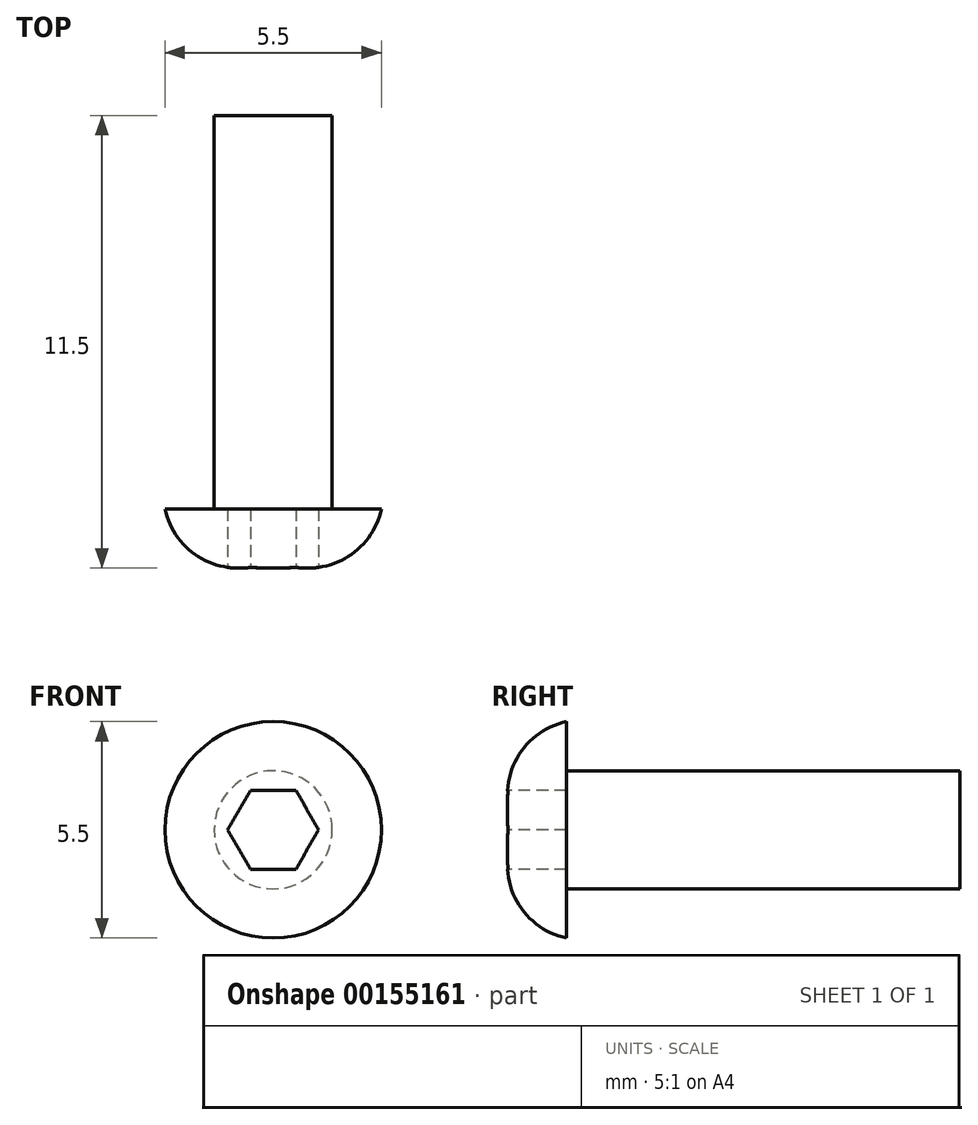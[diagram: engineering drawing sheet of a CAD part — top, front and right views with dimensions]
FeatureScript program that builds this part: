
annotation { "Feature Type Name" : "Feature", "Feature Type Description" : "" }
export const myFeature = defineFeature(function(context is Context, id is Id, definition is map)
    precondition{}
    {
        {
            var Q0;
            Q0=qCreatedBy(makeId("Front.planeOp"),FACE);
            var sketch = newSketch(context, id + "F0", { "sketchPlane" : qUnion([Q0])});
            skCircle(sketch, "E0", {"center": v(0, 0) * mm, "radius": 1.5 * mm});
            skSolve(sketch);
        }
        {
            var Q0;
            Q0=makeQuery(id+"F0.imprint","IMPRINT",FACE,{"disambiguationData":[TD([[makeQuery(id+"F0.imprint","IMPRINT",EDGE,{"derivedFrom":sQuery(id+"F0.wireOp",EDGE,"E0")}),1.0]])]});
            extrude(context, id + "F1", {"entities" : qUnion([Q0]), "depth" : 10 * mm});
        }
        {
            var Q0;
            Q0=makeQuery(id+"F1.opExtrude","CAP_FACE",FACE,{"disambiguationData":[OSD([sQuery(id+"F0.wireOp",EDGE,"E0")])],"isStart":false});
            var sketch = newSketch(context, id + "F2", { "sketchPlane" : qUnion([Q0])});
            skCircle(sketch, "E1", {"center": v(0, 0) * mm, "radius": 2.75 * mm});
            skSolve(sketch);
        }
        {
            var Q0;
            Q0 = qSketchRegion(id + "F2", true);
            extrude(context, id + "F3", {"entities" : qUnion([Q0]), "operationType" : NewBodyOperationType.ADD, "depth" : 1.5 * mm});
        }
        {
            var Q0;
            Q0=makeQuery(id+"F3.opExtrude","CAP_FACE",FACE,{"disambiguationData":[OSD([sQuery(id+"F2.wireOp",EDGE,"E1")])],"isStart":false});
            var sketch = newSketch(context, id + "F4", { "sketchPlane" : qUnion([Q0])});
            skCircle(sketch, "E2.cCircle", {"center": v(0, 0) * mm, "radius": 1 * mm, "construction": true});
            skLineSegment(sketch, "E2.0", {"start": v(0.58, -1) * mm, "end": v(-0.58, -1) * mm});
            skLineSegment(sketch, "E2.1", {"start": v(-0.58, -1) * mm, "end": v(-1.15, 0) * mm});
            skLineSegment(sketch, "E2.2", {"start": v(-1.15, 0) * mm, "end": v(-0.58, 1) * mm});
            skLineSegment(sketch, "E2.3", {"start": v(-0.58, 1) * mm, "end": v(0.58, 1) * mm});
            skLineSegment(sketch, "E2.4", {"start": v(0.58, 1) * mm, "end": v(1.15, 0) * mm});
            skLineSegment(sketch, "E2.5", {"start": v(1.15, 0) * mm, "end": v(0.58, -1) * mm});
            skPoint(sketch, "E2.0.midPoint", {"position": v(0, -1) * mm});
            skSolve(sketch);
        }
        {
            var Q0;
            Q0 = qSketchRegion(id + "F4", true);
            extrude(context, id + "F5", {"entities" : qUnion([Q0]), "operationType" : NewBodyOperationType.REMOVE, "oppositeDirection" : true, "depth" : 1.5 * mm});
        }
        {
            var Q0;
            Q0=makeQuery(id+"F3.opExtrude","CAP_EDGE",EDGE,{"disambiguationData":[OSD([sQuery(id+"F2.wireOp",EDGE,"E1")])],"isStart":false});
            fillet(context, id + "F6", {"entities" : qUnion([Q0]), "radius" : 1.9 * mm, "tangentPropagation" : true, "allowEdgeOverflow" : false});
        }
    });
